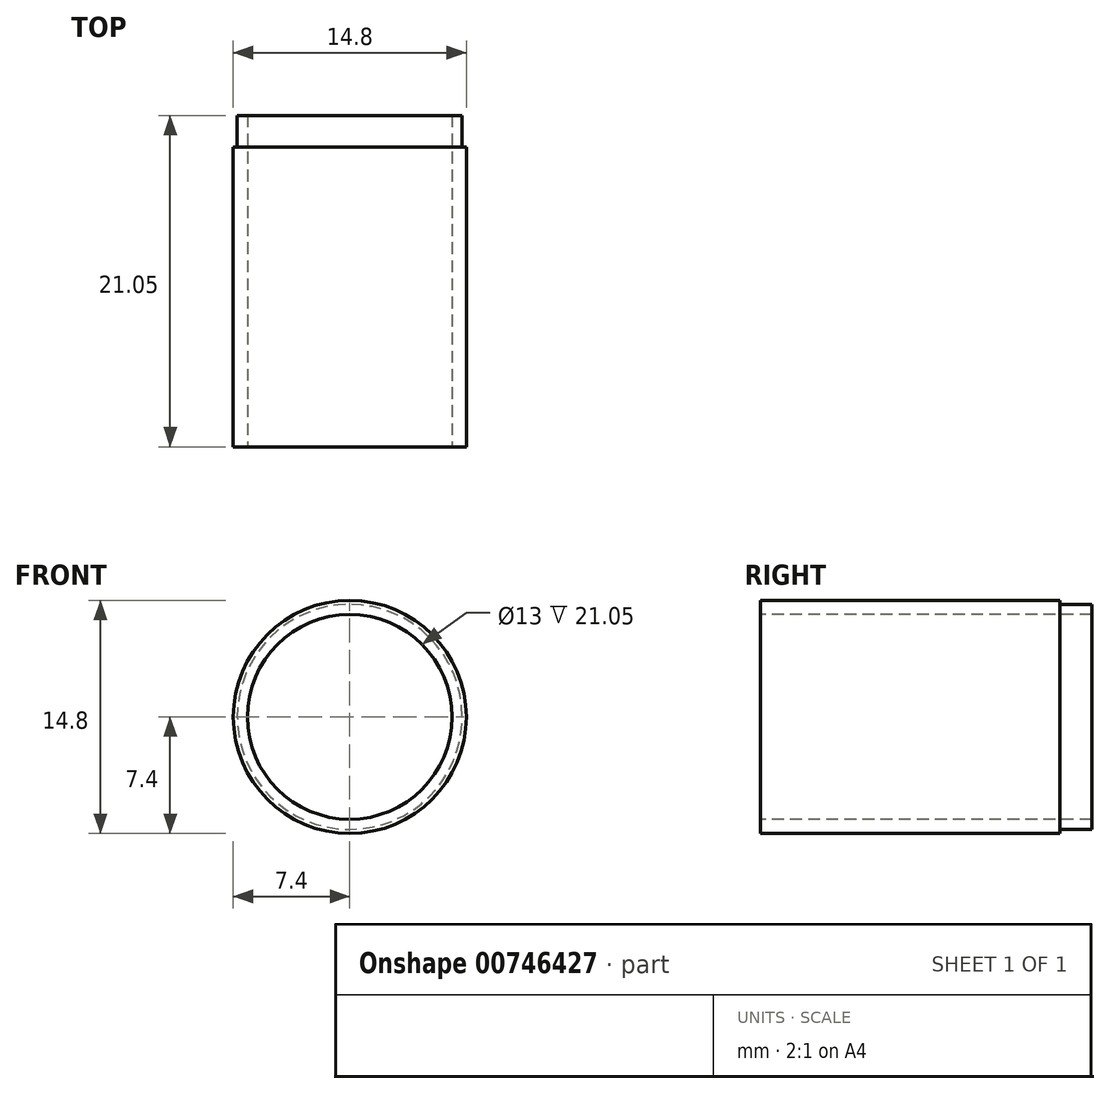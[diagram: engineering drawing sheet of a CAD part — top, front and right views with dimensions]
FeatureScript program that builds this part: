
annotation { "Feature Type Name" : "Feature", "Feature Type Description" : "" }
export const myFeature = defineFeature(function(context is Context, id is Id, definition is map)
    precondition{}
    {
        {
            var Q0;
            Q0=qCreatedBy(makeId("Top.planeOp"),FACE);
            var sketch = newSketch(context, id + "F0", { "sketchPlane" : qUnion([Q0])});
            skCircle(sketch, "E0", {"center": v(0, 0) * mm, "radius": 6.5 * mm});
            skCircle(sketch, "E1", {"center": v(0, 0) * mm, "radius": 7.4 * mm});
            skSolve(sketch);
        }
        {
            var Q0;
            Q0 = qSketchRegion(id + "F0", true);
            extrude(context, id + "F1", {"entities" : qUnion([Q0]), "depth" : 19.05 * mm, "offsetDistance" : 25.4 * mm});
        }
        {
            var Q0;
            Q0=makeQuery(id+"F1.opExtrude","CAP_FACE",FACE,{"disambiguationData":[OSD([sQuery(id+"F0.wireOp",EDGE,"E0"),sQuery(id+"F0.wireOp",EDGE,"E1")])],"isStart":false});
            var sketch = newSketch(context, id + "F2", { "sketchPlane" : qUnion([Q0])});
            skCircle(sketch, "E2", {"center": v(0, 0) * mm, "radius": 6.5 * mm});
            skCircle(sketch, "E3", {"center": v(0, 0) * mm, "radius": 7.14 * mm});
            skSolve(sketch);
        }
        {
            var Q0;
            Q0 = qSketchRegion(id + "F2", true);
            extrude(context, id + "F3", {"entities" : qUnion([Q0]), "operationType" : NewBodyOperationType.ADD, "depth" : 2 * mm, "offsetDistance" : 25.4 * mm});
        }
        {
            var Q0;
            Q0=qCreatedBy(makeId("Top.planeOp"),FACE);
            var sketch = newSketch(context, id + "F4", { "sketchPlane" : qUnion([Q0])});
            skLineSegment(sketch, "E4", {"start": v(-20.28, 0) * mm, "end": v(30.8, 0) * mm});
            skSolve(sketch);
        }
        {
            var Q0;
            Q0=makeQuery(id+"F1.opExtrude","SWEPT_BODY",BODY,{"disambiguationData":[OSD([sQuery(id+"F0.wireOp",EDGE,"E0"),sQuery(id+"F0.wireOp",EDGE,"E1")])]});
            var Q1;
            Q1=sQuery(id+"F4.wireOp",EDGE,"E4");
            transform(context, id + "F5", {"entities" : qUnion([Q0]), "transformType" : TransformType.ROTATION, "transformAxis" : qUnion([Q1]), "angle" : 90 * degree, "oppositeDirection" : true, "makeCopy" : false});
        }
    });
